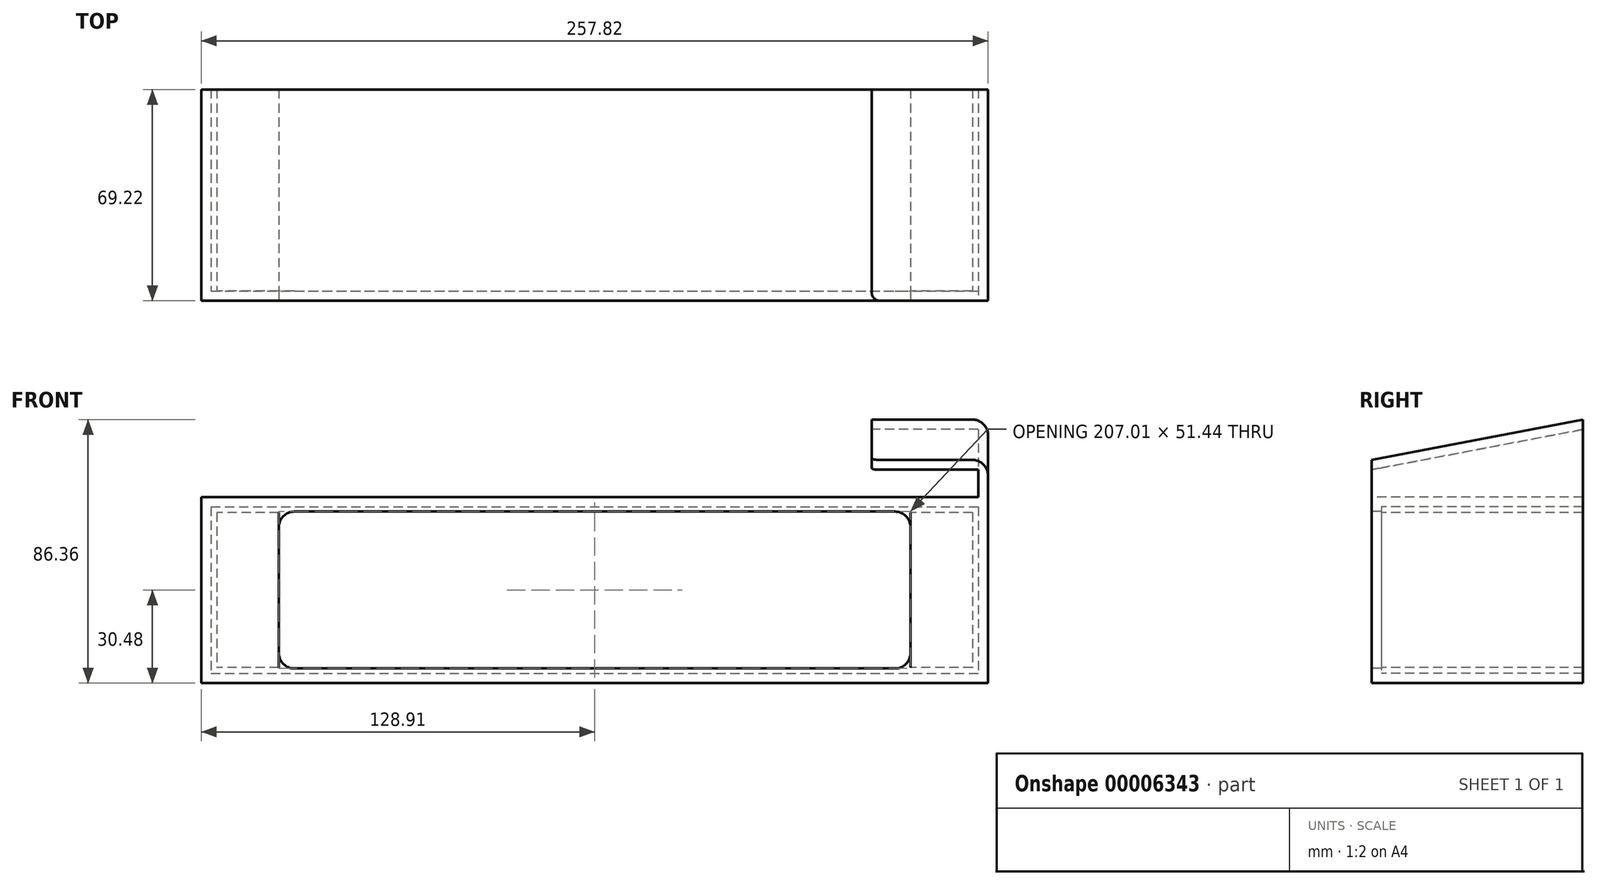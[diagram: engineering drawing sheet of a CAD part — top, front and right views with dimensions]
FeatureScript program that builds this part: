
annotation { "Feature Type Name" : "Feature", "Feature Type Description" : "" }
export const myFeature = defineFeature(function(context is Context, id is Id, definition is map)
    precondition{}
    {
        {
            var Q0;
            Q0=qCreatedBy(makeId("Top.planeOp"),FACE);
            var sketch = newSketch(context, id + "F0", { "sketchPlane" : qUnion([Q0])});
            skLineSegment(sketch, "E0.bottom", {"start": v(123.83, 33.02) * mm, "end": v(-123.83, 33.02) * mm});
            skLineSegment(sketch, "E0.top", {"start": v(123.82, -33.02) * mm, "end": v(-123.82, -33.02) * mm});
            skLineSegment(sketch, "E0.left", {"start": v(123.83, 33.02) * mm, "end": v(123.83, -33.02) * mm});
            skLineSegment(sketch, "E0.right", {"start": v(-123.83, 33.02) * mm, "end": v(-123.83, -33.02) * mm});
            skPoint(sketch, "E0.middle", {"position": v(0, 0) * mm});
            skSolve(sketch);
        }
        {
            var Q0;
            Q0 = qSketchRegion(id + "F0", true);
            extrude(context, id + "F1", {"entities" : qUnion([Q0]), "depth" : 50.8 * mm, "offsetDistance" : 25.4 * mm});
        }
        {
            var Q0;
            Q0=makeQuery(id+"F1.opExtrude","SWEPT_FACE",FACE,{"disambiguationData":[OSD([sQuery(id+"F0.wireOp",EDGE,"E0.top")])]});
            var sketch = newSketch(context, id + "F2", { "sketchPlane" : qUnion([Q0])});
            skLineSegment(sketch, "E1.bottom", {"start": v(-125.73, 52.7) * mm, "end": v(125.73, 52.7) * mm});
            skLineSegment(sketch, "E1.top", {"start": v(-125.73, -1.9) * mm, "end": v(125.73, -1.9) * mm});
            skLineSegment(sketch, "E1.left", {"start": v(-125.73, 52.7) * mm, "end": v(-125.73, -1.9) * mm});
            skLineSegment(sketch, "E1.right", {"start": v(125.73, 52.7) * mm, "end": v(125.73, -1.9) * mm});
            skPoint(sketch, "E1.middle", {"position": v(0, 25.4) * mm});
            skSolve(sketch);
        }
        {
            var Q0;
            Q0 = qSketchRegion(id + "F2", true);
            extrude(context, id + "F3", {"entities" : qUnion([Q0]), "oppositeDirection" : true, "depth" : 66.04 * mm, "offsetDistance" : 25.4 * mm});
        }
        {
            var Q0;
            Q0=makeQuery(id+"F3.opExtrude","CAP_FACE",FACE,{"disambiguationData":[OSD([sQuery(id+"F2.wireOp",EDGE,"E1.bottom"),sQuery(id+"F2.wireOp",EDGE,"E1.top"),sQuery(id+"F2.wireOp",EDGE,"E1.left"),sQuery(id+"F2.wireOp",EDGE,"E1.right")])],"isStart":false});
            shell(context, id + "F4", {"entities" : qUnion([Q0]), "thickness" : 3.17 * mm, "oppositeDirection" : true});
        }
        {
            var Q0;
            Q0=makeQuery(id+"F3.opExtrude","CAP_FACE",FACE,{"disambiguationData":[OSD([sQuery(id+"F2.wireOp",EDGE,"E1.bottom"),sQuery(id+"F2.wireOp",EDGE,"E1.top"),sQuery(id+"F2.wireOp",EDGE,"E1.left"),sQuery(id+"F2.wireOp",EDGE,"E1.right")])],"isStart":true});
            var sketch = newSketch(context, id + "F5", { "sketchPlane" : qUnion([Q0])});
            skLineSegment(sketch, "E2.0", {"start": v(-103.5, 51.12) * mm, "end": v(103.5, 51.12) * mm});
            skLineSegment(sketch, "E2.1", {"start": v(-103.5, 51.12) * mm, "end": v(-103.5, -0.32) * mm});
            skLineSegment(sketch, "E2.2", {"start": v(-103.5, -0.32) * mm, "end": v(103.5, -0.32) * mm});
            skLineSegment(sketch, "E2.3", {"start": v(103.5, 51.12) * mm, "end": v(103.5, -0.32) * mm});
            skSolve(sketch);
        }
        {
            var Q0;
            Q0 = qSketchRegion(id + "F5", true);
            extrude(context, id + "F6", {"entities" : qUnion([Q0]), "operationType" : NewBodyOperationType.REMOVE, "endBound" : BoundingType.THROUGH_ALL, "oppositeDirection" : true, "depth" : 25.4 * mm, "offsetDistance" : 25.4 * mm});
        }
        {
            var Q0;
            Q0=makeQuery(id+"F6.boolean.opBoolean","COPY",EDGE,{"derivedFrom":makeQuery(id+"F6.opExtrude","SWEPT_EDGE",EDGE,{"disambiguationData":[OSD([sQuery(id+"F5.wireOp",EDGE,"E2.1"),sQuery(id+"F5.wireOp",EDGE,"E2.2")])]})});
            var Q1;
            Q1=makeQuery(id+"F6.boolean.opBoolean","COPY",EDGE,{"derivedFrom":makeQuery(id+"F6.opExtrude","SWEPT_EDGE",EDGE,{"disambiguationData":[OSD([sQuery(id+"F5.wireOp",EDGE,"E2.0"),sQuery(id+"F5.wireOp",EDGE,"E2.1")])]})});
            var Q2;
            Q2=makeQuery(id+"F6.boolean.opBoolean","COPY",EDGE,{"derivedFrom":makeQuery(id+"F6.opExtrude","SWEPT_EDGE",EDGE,{"disambiguationData":[OSD([sQuery(id+"F5.wireOp",EDGE,"E2.2"),sQuery(id+"F5.wireOp",EDGE,"E2.3")])]})});
            var Q3;
            Q3=makeQuery(id+"F6.boolean.opBoolean","COPY",EDGE,{"derivedFrom":makeQuery(id+"F6.opExtrude","SWEPT_EDGE",EDGE,{"disambiguationData":[OSD([sQuery(id+"F5.wireOp",EDGE,"E2.0"),sQuery(id+"F5.wireOp",EDGE,"E2.3")])]})});
            fillet(context, id + "F7", {"entities" : qUnion([Q0, Q1, Q2, Q3]), "radius" : 5.08 * mm, "tangentPropagation" : true, "allowEdgeOverflow" : false});
        }
        {
            var Q0;
            Q0=makeQuery(id+"F3.opExtrude","SWEPT_FACE",FACE,{"disambiguationData":[OSD([sQuery(id+"F2.wireOp",EDGE,"E1.right")])]});
            var sketch = newSketch(context, id + "F8", { "sketchPlane" : qUnion([Q0])});
            skLineSegment(sketch, "E3", {"start": v(-36.2, 55.88) * mm, "end": v(-36.2, 68.07) * mm});
            skLineSegment(sketch, "E4", {"start": v(-36.2, 68.07) * mm, "end": v(33.02, 81.28) * mm});
            skLineSegment(sketch, "E5", {"start": v(33.02, 81.28) * mm, "end": v(33.02, 55.88) * mm});
            skLineSegment(sketch, "E6", {"start": v(33.02, 55.88) * mm, "end": v(-36.2, 55.88) * mm});
            skSolve(sketch);
        }
        {
            var Q0;
            Q0=makeQuery(id+"F8.imprint","IMPRINT",FACE,{"disambiguationData":[TD([[makeQuery(id+"F8.imprint","IMPRINT",EDGE,{"derivedFrom":sQuery(id+"F8.wireOp",EDGE,"E3")}),-1.0]])]});
            extrude(context, id + "F9", {"entities" : qUnion([Q0]), "operationType" : NewBodyOperationType.ADD, "oppositeDirection" : true, "depth" : 3.17 * mm, "offsetDistance" : 25.4 * mm});
        }
        {
            var Q0;
            Q0=makeQuery(id+"F9.opExtrude","SWEPT_FACE",FACE,{"disambiguationData":[OSD([sQuery(id+"F8.wireOp",EDGE,"E4")])]});
            var sketch = newSketch(context, id + "F10", { "sketchPlane" : qUnion([Q0])});
            skLineSegment(sketch, "E7.bottom", {"start": v(128.9, -22.8) * mm, "end": v(90.8, -22.8) * mm});
            skLineSegment(sketch, "E7.top", {"start": v(128.9, 47.67) * mm, "end": v(90.8, 47.67) * mm});
            skLineSegment(sketch, "E7.left", {"start": v(128.9, -22.8) * mm, "end": v(128.9, 47.67) * mm});
            skLineSegment(sketch, "E7.right", {"start": v(90.8, -22.8) * mm, "end": v(90.8, 47.67) * mm});
            skSolve(sketch);
        }
        {
            var Q0;
            {var subQ2=sQuery(id+"F10.wireOp",EDGE,"E7.right");Q0=makeQuery(id+"F10.imprint","IMPRINT",FACE,{"disambiguationData":[TD([[makeQuery(id+"F10.imprint","IMPRINT",EDGE,{"derivedFrom":subQ2}),-1.0]])]});}
            var Q1;
            {var subQ0=sQuery(id+"F10.wireOp",EDGE,"E7.left");Q1=makeQuery(id+"F10.imprint","IMPRINT",FACE,{"disambiguationData":[TD([[makeQuery(id+"F10.imprint","IMPRINT",EDGE,{"derivedFrom":subQ0}),1.0]])]});}
            extrude(context, id + "F11", {"entities" : qUnion([Q0, Q1]), "operationType" : NewBodyOperationType.ADD, "oppositeDirection" : true, "depth" : 3.17 * mm, "offsetDistance" : 25.4 * mm});
        }
        {
            var Q0;
            Q0=makeQuery(id+"F11.opExtrude","SWEPT_FACE",FACE,{"disambiguationData":[OSD([sQuery(id+"F10.wireOp",EDGE,"E7.bottom")])]});
            var Q1;
            Q1=makeQuery(id+"F9.boolean.opBoolean","MERGE",FACE,{"derivedFrom":[makeQuery(id+"F3.opExtrude","CAP_FACE",FACE,{"disambiguationData":[OSD([sQuery(id+"F2.wireOp",EDGE,"E1.bottom"),sQuery(id+"F2.wireOp",EDGE,"E1.top"),sQuery(id+"F2.wireOp",EDGE,"E1.left"),sQuery(id+"F2.wireOp",EDGE,"E1.right")])],"isStart":true}),makeQuery(id+"F9.opExtrude","SWEPT_FACE",FACE,{"disambiguationData":[OSD([sQuery(id+"F8.wireOp",EDGE,"E3")])]})]});
            extrude(context, id + "F12", {"entities" : qUnion([Q0]), "operationType" : NewBodyOperationType.ADD, "endBound" : BoundingType.UP_TO_SURFACE, "depth" : 25.4 * mm, "endBoundEntityFace" : qUnion([Q1]), "offsetDistance" : 25.4 * mm});
        }
        {
            var Q0;
            Q0=makeQuery(id+"F11.opExtrude","SWEPT_FACE",FACE,{"disambiguationData":[OSD([sQuery(id+"F10.wireOp",EDGE,"E7.top")])]});
            var Q1;
            Q1=makeQuery(id+"F9.boolean.opBoolean","MERGE",FACE,{"derivedFrom":[makeQuery(id+"F3.opExtrude","CAP_FACE",FACE,{"disambiguationData":[OSD([sQuery(id+"F2.wireOp",EDGE,"E1.bottom"),sQuery(id+"F2.wireOp",EDGE,"E1.top"),sQuery(id+"F2.wireOp",EDGE,"E1.left"),sQuery(id+"F2.wireOp",EDGE,"E1.right")])],"isStart":false}),makeQuery(id+"F9.opExtrude","SWEPT_FACE",FACE,{"disambiguationData":[OSD([sQuery(id+"F8.wireOp",EDGE,"E5")])]})]});
            extrude(context, id + "F13", {"entities" : qUnion([Q0]), "operationType" : NewBodyOperationType.REMOVE, "endBound" : BoundingType.UP_TO_SURFACE, "oppositeDirection" : true, "depth" : 25.4 * mm, "endBoundEntityFace" : qUnion([Q1]), "offsetDistance" : 25.4 * mm});
        }
        {
            var Q0;
            {var subQ0=sQuery(id+"F10.wireOp",EDGE,"E7.right");var subQ1=sQuery(id+"F10.wireOp",EDGE,"E7.left");var subQ2=sQuery(id+"F10.wireOp",EDGE,"E7.top");var subQ3=sQuery(id+"F10.wireOp",EDGE,"E7.bottom");var subQ4=sQuery(id+"F8.wireOp",EDGE,"c5de5143-2929-4ba5-9c82-483c7a732b13.3");var subQ5=sQuery(id+"F8.wireOp",EDGE,"c5de5143-2929-4ba5-9c82-483c7a732b13.2");var subQ6=sQuery(id+"F8.wireOp",EDGE,"c5de5143-2929-4ba5-9c82-483c7a732b13.1");var subQ7=sQuery(id+"F8.wireOp",EDGE,"c5de5143-2929-4ba5-9c82-483c7a732b13.0");var subQ8=sQuery(id+"F8.wireOp",EDGE,"E6");var subQ9=sQuery(id+"F8.wireOp",EDGE,"E5");var subQ10=sQuery(id+"F8.wireOp",EDGE,"E4");var subQ11=sQuery(id+"F8.wireOp",EDGE,"E3");Q0=makeQuery(id+"F12.boolean.opBoolean","MERGE",EDGE,{"derivedFrom":[makeQuery(id+"F11.boolean.opBoolean","INTERSECT",EDGE,{"derivedFrom":[makeQuery(id+"F9.opExtrude","CAP_FACE",FACE,{"disambiguationData":[OSD([subQ11,subQ10,subQ9,subQ8,subQ7,subQ6,subQ5,subQ4])],"isStart":false}),makeQuery(id+"F11.opExtrude","CAP_FACE",FACE,{"disambiguationData":[OSD([subQ3,subQ2,subQ1,subQ0])],"isStart":false})]}),makeQuery(id+"F12.opExtrude","SWEPT_EDGE",EDGE,{"disambiguationData":[OSD([subQ11,subQ10,subQ9,subQ8,subQ7,subQ6,subQ5,subQ4,subQ3,subQ2,subQ1,subQ0])]})]});}
            var Q1;
            Q1=makeQuery(id+"F9.opExtrude","CAP_EDGE",EDGE,{"disambiguationData":[OSD([sQuery(id+"F8.wireOp",EDGE,"E4")])],"isStart":true});
            fillet(context, id + "F14", {"entities" : qUnion([Q0, Q1]), "radius" : 5.08 * mm, "tangentPropagation" : true, "allowEdgeOverflow" : false});
        }
        {
            var Q0;
            Q0=makeQuery(id+"F9.opExtrude","SWEPT_EDGE",EDGE,{"disambiguationData":[OSD([sQuery(id+"F8.wireOp",EDGE,"c5de5143-2929-4ba5-9c82-483c7a732b13.0"),sQuery(id+"F8.wireOp",EDGE,"c5de5143-2929-4ba5-9c82-483c7a732b13.3")])]});
            var Q1;
            Q1=makeQuery(id+"F9.opExtrude","SWEPT_EDGE",EDGE,{"disambiguationData":[OSD([sQuery(id+"F8.wireOp",EDGE,"c5de5143-2929-4ba5-9c82-483c7a732b13.0"),sQuery(id+"F8.wireOp",EDGE,"c5de5143-2929-4ba5-9c82-483c7a732b13.1")])]});
            var Q2;
            Q2=makeQuery(id+"F13.boolean.opBoolean","COPY",EDGE,{"derivedFrom":makeQuery(id+"F13.opExtrude","TWEAK_EDGE",EDGE,{"derivedFrom":[makeQuery(id+"F11.opExtrude","SWEPT_EDGE",EDGE,{"disambiguationData":[OSD([sQuery(id+"F10.wireOp",EDGE,"E7.top"),sQuery(id+"F10.wireOp",EDGE,"E7.right")])]}),makeQuery(id+"F9.boolean.opBoolean","MERGE",FACE,{"derivedFrom":[makeQuery(id+"F3.opExtrude","CAP_FACE",FACE,{"disambiguationData":[OSD([sQuery(id+"F2.wireOp",EDGE,"E1.bottom"),sQuery(id+"F2.wireOp",EDGE,"E1.top"),sQuery(id+"F2.wireOp",EDGE,"E1.left"),sQuery(id+"F2.wireOp",EDGE,"E1.right")])],"isStart":false}),makeQuery(id+"F9.opExtrude","SWEPT_FACE",FACE,{"disambiguationData":[OSD([sQuery(id+"F8.wireOp",EDGE,"E5")])]})]})]})});
            var Q3;
            Q3=makeQuery(id+"F12.opExtrude","TWEAK_EDGE",EDGE,{"derivedFrom":[makeQuery(id+"F9.boolean.opBoolean","MERGE",FACE,{"derivedFrom":[makeQuery(id+"F3.opExtrude","CAP_FACE",FACE,{"disambiguationData":[OSD([sQuery(id+"F2.wireOp",EDGE,"E1.bottom"),sQuery(id+"F2.wireOp",EDGE,"E1.top"),sQuery(id+"F2.wireOp",EDGE,"E1.left"),sQuery(id+"F2.wireOp",EDGE,"E1.right")])],"isStart":true}),makeQuery(id+"F9.opExtrude","SWEPT_FACE",FACE,{"disambiguationData":[OSD([sQuery(id+"F8.wireOp",EDGE,"E3")])]})]}),makeQuery(id+"F11.opExtrude","SWEPT_EDGE",EDGE,{"disambiguationData":[OSD([sQuery(id+"F10.wireOp",EDGE,"E7.bottom"),sQuery(id+"F10.wireOp",EDGE,"E7.right")])]})]});
            var Q4;
            Q4=makeQuery(id+"F9.opExtrude","SWEPT_EDGE",EDGE,{"disambiguationData":[OSD([sQuery(id+"F8.wireOp",EDGE,"c5de5143-2929-4ba5-9c82-483c7a732b13.2"),sQuery(id+"F8.wireOp",EDGE,"c5de5143-2929-4ba5-9c82-483c7a732b13.3")])]});
            var Q5;
            Q5=makeQuery(id+"F9.opExtrude","SWEPT_EDGE",EDGE,{"disambiguationData":[OSD([sQuery(id+"F8.wireOp",EDGE,"c5de5143-2929-4ba5-9c82-483c7a732b13.1"),sQuery(id+"F8.wireOp",EDGE,"c5de5143-2929-4ba5-9c82-483c7a732b13.2")])]});
            fillet(context, id + "F15", {"entities" : qUnion([Q0, Q1, Q2, Q3, Q4, Q5]), "radius" : 2.54 * mm, "tangentPropagation" : true, "allowEdgeOverflow" : false});
        }
    });
